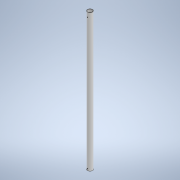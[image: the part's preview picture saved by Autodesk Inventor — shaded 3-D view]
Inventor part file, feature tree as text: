
AUTODESK INVENTOR PART (.ipt)
format: ipt  version: 2022 (Build 260153000, 153)  size: 174,080 bytes
history: native  units: mm
features: extrude x2, sketch x2
ambient origin geometry x8: Origin, YZ Plane, XZ Plane, XY Plane, X Axis, Y Axis, Z Axis, Center Point
bodies: Body1 (feature_tree)
feature tree (4):
  extrude  "Extrusion5"  Depth=18.0mm
  extrude  "Extrusion6"  Depth=10.0mm TaperAngle=0.0deg
  sketch  "Sketch2"  dims[d31=34.456mm d91=18.0mm]
  sketch  "Sketch3"  dims[d92=16.0mm d93=500.0mm d94=0.0mm d95=6.0mm d96=3.0mm d97=16.0mm d98=3.0mm d99=10.0mm d100=10.0mm d101=0.0mm d102=0.0mm]
